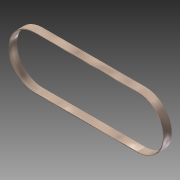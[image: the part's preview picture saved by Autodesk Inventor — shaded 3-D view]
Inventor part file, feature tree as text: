
AUTODESK INVENTOR PART (.ipt)
format: ipt  version: 2014 SP1 (Build 180222100, 222)  size: 90,624 bytes
history: native  units: in
note: dims shown in document units (in); Inventor stores cm internally (conversion verified against a paired STEP export)
features: extrude x1, sketch x1
ambient origin geometry x8: Origin, YZ Plane, XZ Plane, XY Plane, X Axis, Y Axis, Z Axis, Center Point
bodies: Solid1 (feature_tree)
feature tree (2):
  extrude  "Extrusion1"  Depth=0.77in
  sketch  "Sketch1"  dims[d0=2.25in d1=0.77in d2=0.77in d3=0.1181in d4=0.0in]
